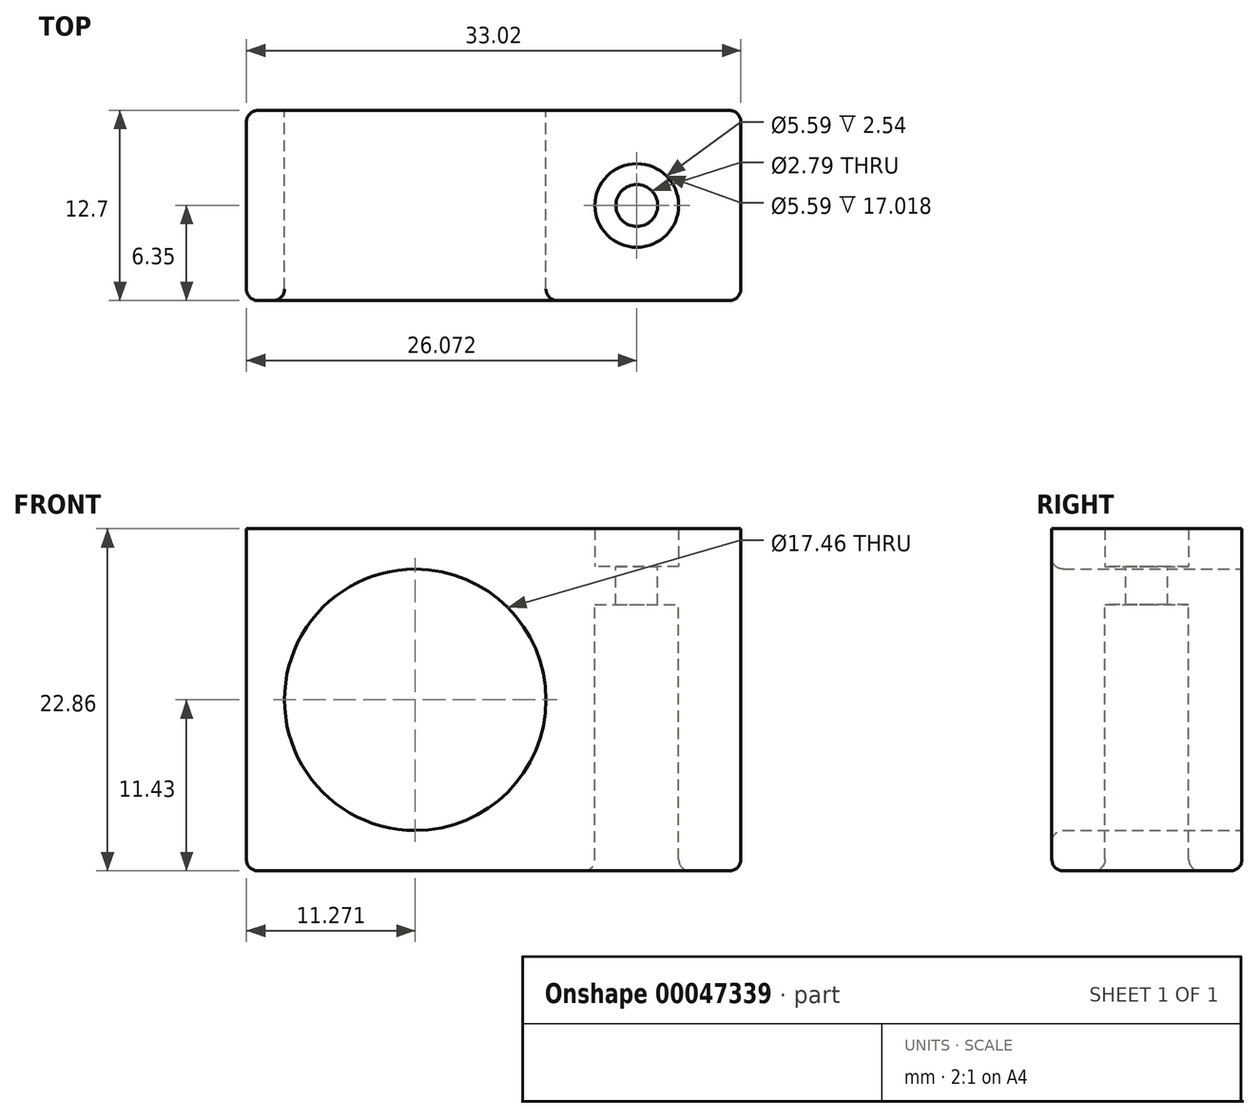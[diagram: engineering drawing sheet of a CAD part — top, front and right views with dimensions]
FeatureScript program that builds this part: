
annotation { "Feature Type Name" : "Feature", "Feature Type Description" : "" }
export const myFeature = defineFeature(function(context is Context, id is Id, definition is map)
    precondition{}
    {
        {
            var Q0;
            Q0=qCreatedBy(makeId("Top.planeOp"),FACE);
            var sketch = newSketch(context, id + "F0", { "sketchPlane" : qUnion([Q0])});
            skLineSegment(sketch, "E0.rect.bottom", {"start": v(16.51, 6.35) * mm, "end": v(-16.51, 6.35) * mm});
            skLineSegment(sketch, "E0.rect.top", {"start": v(16.51, -6.35) * mm, "end": v(-16.51, -6.35) * mm});
            skLineSegment(sketch, "E0.rect.left", {"start": v(16.51, 6.35) * mm, "end": v(16.51, -6.35) * mm});
            skLineSegment(sketch, "E0.rect.right", {"start": v(-16.51, 6.35) * mm, "end": v(-16.51, -6.35) * mm});
            skPoint(sketch, "E0.rect.middle", {"position": v(0, 0) * mm});
            skCircle(sketch, "E1", {"center": v(9.56, 0) * mm, "radius": 2.8 * mm});
            skPoint(sketch, "E1.centerSnap0", {"position": v(16.51, 0) * mm});
            skSolve(sketch);
        }
        {
            var Q0;
            Q0 = qSketchRegion(id + "F0", true);
            extrude(context, id + "F1", {"entities" : qUnion([Q0]), "depth" : 2.54 * mm});
        }
        {
            var Q0;
            Q0=makeQuery(id+"F1.opExtrude","CAP_FACE",FACE,{"disambiguationData":[OSD([sQuery(id+"F0.wireOp",EDGE,"E0.rect.bottom"),sQuery(id+"F0.wireOp",EDGE,"E0.rect.top"),sQuery(id+"F0.wireOp",EDGE,"E0.rect.left"),sQuery(id+"F0.wireOp",EDGE,"E0.rect.right"),sQuery(id+"F0.wireOp",EDGE,"E1")])],"isStart":true});
            var sketch = newSketch(context, id + "F2", { "sketchPlane" : qUnion([Q0])});
            skLineSegment(sketch, "E2.bottom", {"start": v(-16.51, 6.35) * mm, "end": v(16.51, 6.35) * mm});
            skLineSegment(sketch, "E2.top", {"start": v(-16.51, -6.35) * mm, "end": v(16.51, -6.35) * mm});
            skLineSegment(sketch, "E2.left", {"start": v(-16.51, 6.35) * mm, "end": v(-16.51, -6.35) * mm});
            skLineSegment(sketch, "E2.right", {"start": v(16.51, 6.35) * mm, "end": v(16.51, -6.35) * mm});
            skCircle(sketch, "E3", {"center": v(9.56, 0) * mm, "radius": 1.4 * mm});
            skSolve(sketch);
        }
        {
            var Q0;
            Q0 = qSketchRegion(id + "F2", true);
            extrude(context, id + "F3", {"entities" : qUnion([Q0]), "operationType" : NewBodyOperationType.ADD, "depth" : 2.54 * mm});
        }
        {
            var Q0;
            Q0=makeQuery(id+"F3.opExtrude","CAP_FACE",FACE,{"disambiguationData":[OSD([sQuery(id+"F2.wireOp",EDGE,"E2.bottom"),sQuery(id+"F2.wireOp",EDGE,"E2.top"),sQuery(id+"F2.wireOp",EDGE,"E2.left"),sQuery(id+"F2.wireOp",EDGE,"E2.right"),sQuery(id+"F2.wireOp",EDGE,"E3")])],"isStart":false});
            var sketch = newSketch(context, id + "F4", { "sketchPlane" : qUnion([Q0])});
            skLineSegment(sketch, "E4.bottom", {"start": v(-16.51, 6.35) * mm, "end": v(16.51, 6.35) * mm});
            skLineSegment(sketch, "E4.top", {"start": v(-16.51, -6.35) * mm, "end": v(16.51, -6.35) * mm});
            skLineSegment(sketch, "E4.left", {"start": v(-16.51, 6.35) * mm, "end": v(-16.51, -6.35) * mm});
            skLineSegment(sketch, "E4.right", {"start": v(16.51, 6.35) * mm, "end": v(16.51, -6.35) * mm});
            skCircle(sketch, "E5", {"center": v(9.56, 0) * mm, "radius": 2.8 * mm});
            skSolve(sketch);
        }
        {
            var Q0;
            Q0 = qSketchRegion(id + "F4", true);
            extrude(context, id + "F5", {"entities" : qUnion([Q0]), "operationType" : NewBodyOperationType.ADD, "depth" : 17.78 * mm});
        }
        {
            var Q0;
            Q0=makeQuery(id+"F5.boolean.opBoolean","MERGE",FACE,{"derivedFrom":[makeQuery(id+"F3.boolean.opBoolean","MERGE",FACE,{"derivedFrom":[makeQuery(id+"F1.opExtrude","SWEPT_FACE",FACE,{"disambiguationData":[OSD([sQuery(id+"F0.wireOp",EDGE,"E0.rect.bottom")])]}),makeQuery(id+"F3.opExtrude","SWEPT_FACE",FACE,{"disambiguationData":[OSD([sQuery(id+"F2.wireOp",EDGE,"E2.top")])]})]}),makeQuery(id+"F5.opExtrude","SWEPT_FACE",FACE,{"disambiguationData":[OSD([sQuery(id+"F4.wireOp",EDGE,"E4.top")])]})]});
            var sketch = newSketch(context, id + "F6", { "sketchPlane" : qUnion([Q0])});
            skCircle(sketch, "E6", {"center": v(5.24, -8.9) * mm, "radius": 8.73 * mm});
            skPoint(sketch, "E6.centerSnap0", {"position": v(16.51, -8.9) * mm});
            skLineSegment(sketch, "E7", {"start": v(16.51, -8.9) * mm, "end": v(13.97, -8.9) * mm, "construction": true});
            skSolve(sketch);
        }
        {
            var Q0;
            Q0=makeQuery(id+"F6.imprint","IMPRINT",FACE,{"disambiguationData":[TD([[makeQuery(id+"F6.imprint","IMPRINT",EDGE,{"derivedFrom":sQuery(id+"F6.wireOp",EDGE,"E6")}),1.0]])]});
            extrude(context, id + "F7", {"entities" : qUnion([Q0]), "operationType" : NewBodyOperationType.REMOVE, "endBound" : BoundingType.THROUGH_ALL, "oppositeDirection" : true, "depth" : 25.4 * mm});
        }
        {
            var Q0;
            Q0=makeQuery(id+"F7.boolean.opBoolean","INTERSECT",EDGE,{"derivedFrom":[makeQuery(id+"F5.boolean.opBoolean","MERGE",FACE,{"derivedFrom":[makeQuery(id+"F3.boolean.opBoolean","MERGE",FACE,{"derivedFrom":[makeQuery(id+"F1.opExtrude","SWEPT_FACE",FACE,{"disambiguationData":[OSD([sQuery(id+"F0.wireOp",EDGE,"E0.rect.top")])]}),makeQuery(id+"F3.opExtrude","SWEPT_FACE",FACE,{"disambiguationData":[OSD([sQuery(id+"F2.wireOp",EDGE,"E2.bottom")])]})]}),makeQuery(id+"F5.opExtrude","SWEPT_FACE",FACE,{"disambiguationData":[OSD([sQuery(id+"F4.wireOp",EDGE,"E4.bottom")])]})]}),makeQuery(id+"F7.opExtrude","SWEPT_FACE",FACE,{"disambiguationData":[OSD([sQuery(id+"F6.wireOp",EDGE,"E6")])]})]});
            var Q1;
            Q1=makeQuery(id+"F7.boolean.opBoolean","COPY",EDGE,{"derivedFrom":makeQuery(id+"F7.opExtrude","CAP_EDGE",EDGE,{"disambiguationData":[OSD([sQuery(id+"F6.wireOp",EDGE,"E6")])],"isStart":true})});
            fillet(context, id + "F8", {"entities" : qUnion([Q0, Q1]), "radius" : 0.76 * mm, "tangentPropagation" : true, "allowEdgeOverflow" : false});
        }
        {
            var Q0;
            Q0=makeQuery(id+"F5.opExtrude","CAP_EDGE",EDGE,{"disambiguationData":[OSD([sQuery(id+"F4.wireOp",EDGE,"E5")])],"isStart":false});
            fillet(context, id + "F9", {"entities" : qUnion([Q0]), "radius" : 0.76 * mm, "tangentPropagation" : true, "allowEdgeOverflow" : false});
        }
        {
            var Q0;
            Q0=makeQuery(id+"F5.boolean.opBoolean","MERGE",EDGE,{"derivedFrom":[makeQuery(id+"F3.boolean.opBoolean","MERGE",EDGE,{"derivedFrom":[makeQuery(id+"F1.opExtrude","SWEPT_EDGE",EDGE,{"disambiguationData":[OSD([sQuery(id+"F0.wireOp",EDGE,"E0.rect.bottom"),sQuery(id+"F0.wireOp",EDGE,"E0.rect.right")])]}),makeQuery(id+"F3.opExtrude","SWEPT_EDGE",EDGE,{"disambiguationData":[OSD([sQuery(id+"F2.wireOp",EDGE,"E2.top"),sQuery(id+"F2.wireOp",EDGE,"E2.left")])]})]}),makeQuery(id+"F5.opExtrude","SWEPT_EDGE",EDGE,{"disambiguationData":[OSD([sQuery(id+"F4.wireOp",EDGE,"E4.top"),sQuery(id+"F4.wireOp",EDGE,"E4.left")])]})]});
            var Q1;
            Q1=makeQuery(id+"F5.opExtrude","CAP_EDGE",EDGE,{"disambiguationData":[OSD([sQuery(id+"F4.wireOp",EDGE,"E4.left")])],"isStart":false});
            var Q2;
            Q2=makeQuery(id+"F5.boolean.opBoolean","MERGE",EDGE,{"derivedFrom":[makeQuery(id+"F3.boolean.opBoolean","MERGE",EDGE,{"derivedFrom":[makeQuery(id+"F1.opExtrude","SWEPT_EDGE",EDGE,{"disambiguationData":[OSD([sQuery(id+"F0.wireOp",EDGE,"E0.rect.top"),sQuery(id+"F0.wireOp",EDGE,"E0.rect.right")])]}),makeQuery(id+"F3.opExtrude","SWEPT_EDGE",EDGE,{"disambiguationData":[OSD([sQuery(id+"F2.wireOp",EDGE,"E2.bottom"),sQuery(id+"F2.wireOp",EDGE,"E2.left")])]})]}),makeQuery(id+"F5.opExtrude","SWEPT_EDGE",EDGE,{"disambiguationData":[OSD([sQuery(id+"F4.wireOp",EDGE,"E4.bottom"),sQuery(id+"F4.wireOp",EDGE,"E4.left")])]})]});
            var Q3;
            Q3=makeQuery(id+"F5.opExtrude","CAP_EDGE",EDGE,{"disambiguationData":[OSD([sQuery(id+"F4.wireOp",EDGE,"E4.bottom")])],"isStart":false});
            var Q4;
            Q4=makeQuery(id+"F5.opExtrude","CAP_EDGE",EDGE,{"disambiguationData":[OSD([sQuery(id+"F4.wireOp",EDGE,"E4.top")])],"isStart":false});
            var Q5;
            Q5=makeQuery(id+"F5.opExtrude","CAP_EDGE",EDGE,{"disambiguationData":[OSD([sQuery(id+"F4.wireOp",EDGE,"E4.right")])],"isStart":false});
            var Q6;
            Q6=makeQuery(id+"F5.boolean.opBoolean","MERGE",EDGE,{"derivedFrom":[makeQuery(id+"F3.boolean.opBoolean","MERGE",EDGE,{"derivedFrom":[makeQuery(id+"F1.opExtrude","SWEPT_EDGE",EDGE,{"disambiguationData":[OSD([sQuery(id+"F0.wireOp",EDGE,"E0.rect.bottom"),sQuery(id+"F0.wireOp",EDGE,"E0.rect.left")])]}),makeQuery(id+"F3.opExtrude","SWEPT_EDGE",EDGE,{"disambiguationData":[OSD([sQuery(id+"F2.wireOp",EDGE,"E2.top"),sQuery(id+"F2.wireOp",EDGE,"E2.right")])]})]}),makeQuery(id+"F5.opExtrude","SWEPT_EDGE",EDGE,{"disambiguationData":[OSD([sQuery(id+"F4.wireOp",EDGE,"E4.top"),sQuery(id+"F4.wireOp",EDGE,"E4.right")])]})]});
            var Q7;
            Q7=makeQuery(id+"F5.boolean.opBoolean","MERGE",EDGE,{"derivedFrom":[makeQuery(id+"F3.boolean.opBoolean","MERGE",EDGE,{"derivedFrom":[makeQuery(id+"F1.opExtrude","SWEPT_EDGE",EDGE,{"disambiguationData":[OSD([sQuery(id+"F0.wireOp",EDGE,"E0.rect.top"),sQuery(id+"F0.wireOp",EDGE,"E0.rect.left")])]}),makeQuery(id+"F3.opExtrude","SWEPT_EDGE",EDGE,{"disambiguationData":[OSD([sQuery(id+"F2.wireOp",EDGE,"E2.bottom"),sQuery(id+"F2.wireOp",EDGE,"E2.right")])]})]}),makeQuery(id+"F5.opExtrude","SWEPT_EDGE",EDGE,{"disambiguationData":[OSD([sQuery(id+"F4.wireOp",EDGE,"E4.bottom"),sQuery(id+"F4.wireOp",EDGE,"E4.right")])]})]});
            fillet(context, id + "F10", {"entities" : qUnion([Q0, Q1, Q2, Q3, Q4, Q5, Q6, Q7]), "radius" : 0.76 * mm, "tangentPropagation" : true, "allowEdgeOverflow" : false});
        }
    });
